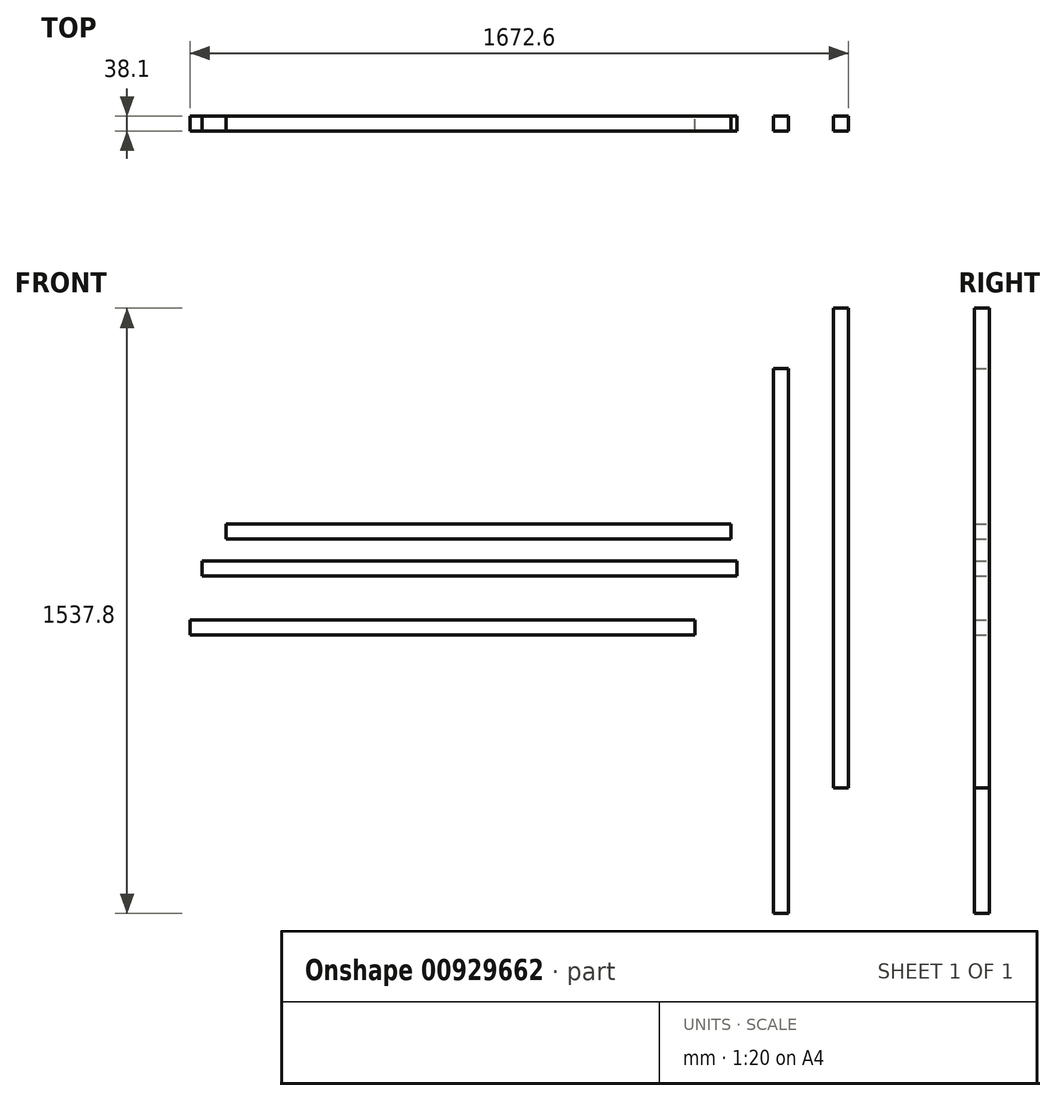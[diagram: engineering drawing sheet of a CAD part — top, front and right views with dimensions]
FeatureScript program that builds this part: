
annotation { "Feature Type Name" : "Feature", "Feature Type Description" : "" }
export const myFeature = defineFeature(function(context is Context, id is Id, definition is map)
    precondition{}
    {
        {
            var Q0;
            Q0=qCreatedBy(makeId("Front.planeOp"),FACE);
            var sketch = newSketch(context, id + "F0", { "sketchPlane" : qUnion([Q0])});
            skLineSegment(sketch, "E0.bottom", {"start": v(471.1, 112.4) * mm, "end": v(-811.6, 112.4) * mm});
            skLineSegment(sketch, "E0.top", {"start": v(471.1, 74.3) * mm, "end": v(-811.6, 74.3) * mm});
            skLineSegment(sketch, "E0.left", {"start": v(471.1, 112.4) * mm, "end": v(471.1, 74.3) * mm});
            skLineSegment(sketch, "E0.right", {"start": v(-811.6, 112.4) * mm, "end": v(-811.6, 74.3) * mm});
            skPoint(sketch, "E0.middle", {"position": v(-170.25, 93.34) * mm});
            skSolve(sketch);
        }
        {
            var Q0;
            Q0=qCreatedBy(makeId("Front.planeOp"),FACE);
            var sketch = newSketch(context, id + "F1", { "sketchPlane" : qUnion([Q0])});
            skLineSegment(sketch, "E1.bottom", {"start": v(487.25, -19.05) * mm, "end": v(-871.65, -19.05) * mm});
            skLineSegment(sketch, "E1.top", {"start": v(487.25, 19.05) * mm, "end": v(-871.65, 19.05) * mm});
            skLineSegment(sketch, "E1.left", {"start": v(487.25, -19.05) * mm, "end": v(487.25, 19.05) * mm});
            skLineSegment(sketch, "E1.right", {"start": v(-871.65, -19.05) * mm, "end": v(-871.65, 19.05) * mm});
            skPoint(sketch, "E1.middle", {"position": v(-192.2, 0) * mm});
            skSolve(sketch);
        }
        {
            var Q0;
            Q0=qCreatedBy(makeId("Front.planeOp"),FACE);
            var sketch = newSketch(context, id + "F2", { "sketchPlane" : qUnion([Q0])});
            skLineSegment(sketch, "E2.bottom", {"start": v(617.66, 507.39) * mm, "end": v(579.56, 507.39) * mm});
            skLineSegment(sketch, "E2.top", {"start": v(617.66, -876.91) * mm, "end": v(579.56, -876.91) * mm});
            skLineSegment(sketch, "E2.left", {"start": v(617.66, 507.39) * mm, "end": v(617.66, -876.91) * mm});
            skLineSegment(sketch, "E2.right", {"start": v(579.56, 507.39) * mm, "end": v(579.56, -876.91) * mm});
            skPoint(sketch, "E2.middle", {"position": v(598.61, -184.76) * mm});
            skSolve(sketch);
        }
        {
            var Q0;
            Q0 = qSketchRegion(id + "F0", true);
            extrude(context, id + "F3", {"entities" : qUnion([Q0]), "depth" : 38.1 * mm, "offsetDistance" : 25.4 * mm});
        }
        {
            var Q0;
            Q0=makeQuery(id+"F1.imprint","IMPRINT",FACE,{"disambiguationData":[TD([[makeQuery(id+"F1.imprint","IMPRINT",EDGE,{"derivedFrom":sQuery(id+"F1.wireOp",EDGE,"E1.bottom")}),-1.0]])]});
            extrude(context, id + "F4", {"entities" : qUnion([Q0]), "depth" : 38.1 * mm, "offsetDistance" : 25.4 * mm});
        }
        {
            var Q0;
            Q0=makeQuery(id+"F2.imprint","IMPRINT",FACE,{"disambiguationData":[TD([[makeQuery(id+"F2.imprint","IMPRINT",EDGE,{"derivedFrom":sQuery(id+"F2.wireOp",EDGE,"E2.bottom")}),1.0]])]});
            extrude(context, id + "F5", {"entities" : qUnion([Q0]), "depth" : 38.1 * mm, "offsetDistance" : 25.4 * mm});
        }
        {
            var Q0;
            Q0=qCreatedBy(makeId("Front.planeOp"),FACE);
            var sketch = newSketch(context, id + "F6", { "sketchPlane" : qUnion([Q0])});
            skLineSegment(sketch, "E3.bottom", {"start": v(380.07, -168.87) * mm, "end": v(-902.63, -168.87) * mm});
            skLineSegment(sketch, "E3.top", {"start": v(380.07, -130.77) * mm, "end": v(-902.63, -130.77) * mm});
            skLineSegment(sketch, "E3.left", {"start": v(380.07, -168.87) * mm, "end": v(380.07, -130.77) * mm});
            skLineSegment(sketch, "E3.right", {"start": v(-902.63, -168.87) * mm, "end": v(-902.63, -130.77) * mm});
            skPoint(sketch, "E3.middle", {"position": v(-261.28, -149.82) * mm});
            skSolve(sketch);
        }
        {
            var Q0;
            Q0=qCreatedBy(makeId("Front.planeOp"),FACE);
            var sketch = newSketch(context, id + "F7", { "sketchPlane" : qUnion([Q0])});
            skLineSegment(sketch, "E4.bottom", {"start": v(769.97, 660.9) * mm, "end": v(731.87, 660.9) * mm});
            skLineSegment(sketch, "E4.top", {"start": v(769.97, -558.3) * mm, "end": v(731.87, -558.3) * mm});
            skLineSegment(sketch, "E4.left", {"start": v(769.97, 660.9) * mm, "end": v(769.97, -558.3) * mm});
            skLineSegment(sketch, "E4.right", {"start": v(731.87, 660.9) * mm, "end": v(731.87, -558.3) * mm});
            skPoint(sketch, "E4.middle", {"position": v(750.92, 51.3) * mm});
            skSolve(sketch);
        }
        {
            var Q0;
            Q0=makeQuery(id+"F6.imprint","IMPRINT",FACE,{"disambiguationData":[TD([[makeQuery(id+"F6.imprint","IMPRINT",EDGE,{"derivedFrom":sQuery(id+"F6.wireOp",EDGE,"E3.bottom")}),-1.0]])]});
            extrude(context, id + "F8", {"entities" : qUnion([Q0]), "depth" : 38.1 * mm, "offsetDistance" : 25.4 * mm});
        }
        {
            var Q0;
            Q0=makeQuery(id+"F7.imprint","IMPRINT",FACE,{"disambiguationData":[TD([[makeQuery(id+"F7.imprint","IMPRINT",EDGE,{"derivedFrom":sQuery(id+"F7.wireOp",EDGE,"E4.bottom")}),1.0]])]});
            extrude(context, id + "F9", {"entities" : qUnion([Q0]), "depth" : 38.1 * mm, "offsetDistance" : 25.4 * mm});
        }
    });
